# Revit family: IRE 125 C1 AC_7900077
name_source: partatom
category: Mechanical Equipment
revit_build: Autodesk Revit MEP 2014 (Build: 20130308_1515(x64)
units: mm (PartAtom-declared; Revit-internal decimal feet)

## types (1)
- IRE 125 C1 AC
    Capacitor = 4 μF
    Current = 1 A
    Depth = 367 mm  [stored 1.20407 ft]
    Description = Insulated duct fans with circular connections
    Diameter = 125 mm  [stored 0.410105 ft]
    Frequency = 50 Hz
    Height = 245 mm  [stored 0.803806 ft]
    Main Material = Steel, Galvanized
    Max. temperature of transported air = 65 °C
    Max. temperature of transported air when speed controlled = 65 °C
    Phase = 1
    Power = 122 W
    Sound pressure level at 3 m = 37 dB(A)
    Speed = 1850 rpm
    Voltage = 230 V
    Voltage range = 220-240 V
    Weight = 9.70 kg
    Width = 483 mm
    Wiring diagram = 4040001

note: [stored X ft] marks values corroborated as IEEE doubles in the binary element streams (Revit-internal decimal feet)

## geometry (parser evidence)
native form markers: Sweep x5
no freeform markers — native parametric forms only
